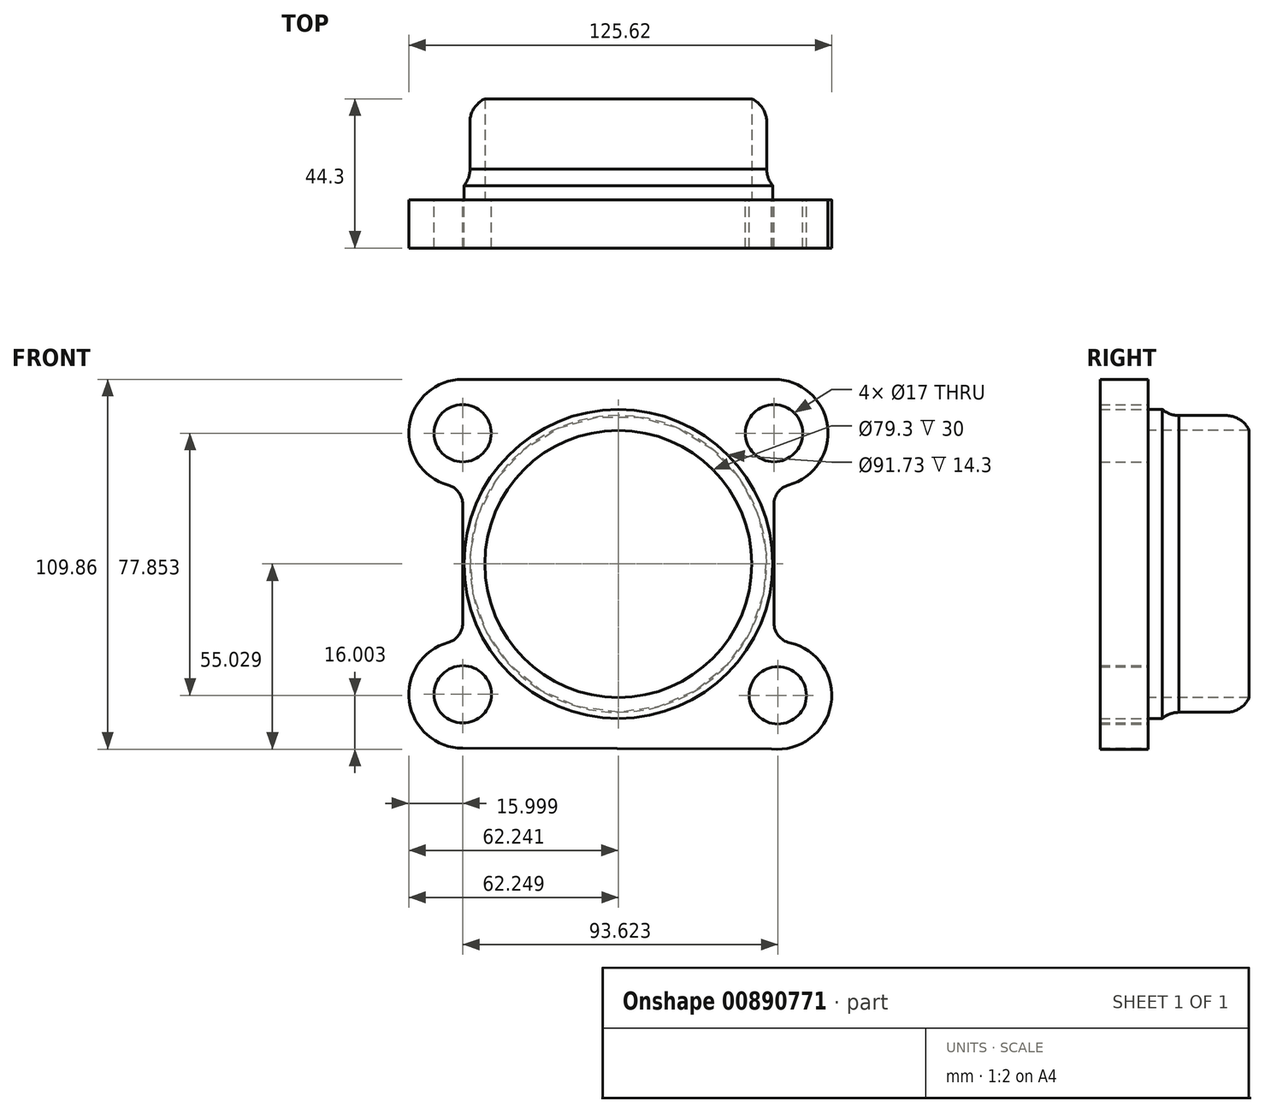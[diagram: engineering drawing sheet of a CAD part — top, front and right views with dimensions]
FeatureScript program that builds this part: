
annotation { "Feature Type Name" : "Feature", "Feature Type Description" : "" }
export const myFeature = defineFeature(function(context is Context, id is Id, definition is map)
    precondition{}
    {
        {
            var Q0;
            Q0=qCreatedBy(makeId("Front.planeOp"),FACE);
            var sketch = newSketch(context, id + "F0", { "sketchPlane" : qUnion([Q0])});
            skArc(sketch, "E0", {"start": v(-184.46, 80.5) * mm, "mid": v(-200.31, 66.69) * mm, "end": v(-188.8, 49.1) * mm});
            skArc(sketch, "E1", {"start": v(-188.8, 2.33) * mm, "mid": v(-200.28, -15.27) * mm, "end": v(-184.43, -29.06) * mm});
            skArc(sketch, "E2", {"start": v(-92.7, -29.25) * mm, "mid": v(-75.07, -16.05) * mm, "end": v(-87.31, 2.25) * mm});
            skArc(sketch, "E3", {"start": v(-87.62, 49.1) * mm, "mid": v(-76.11, 66.69) * mm, "end": v(-91.96, 80.5) * mm});
            skLineSegment(sketch, "E4", {"start": v(-184.43, 43.32) * mm, "end": v(-184.43, 8.1) * mm});
            skLineSegment(sketch, "E5", {"start": v(-92, 8.1) * mm, "end": v(-92, 43.32) * mm});
            skLineSegment(sketch, "E6", {"start": v(-184.46, 80.5) * mm, "end": v(-91.96, 80.5) * mm});
            skLineSegment(sketch, "E7", {"start": v(-184.43, -29.06) * mm, "end": v(-92.7, -29.25) * mm});
            skPoint(sketch, "E8.newPointA", {"position": v(-184.46, 48.5) * mm});
            skArc(sketch, "E8.filletArc", {"start": v(-184.43, 43.32) * mm, "mid": v(-185.65, 46.94) * mm, "end": v(-188.8, 49.1) * mm});
            skPoint(sketch, "E9.newPointA", {"position": v(-184.43, 2.94) * mm});
            skArc(sketch, "E9.filletArc", {"start": v(-188.8, 2.33) * mm, "mid": v(-185.64, 4.48) * mm, "end": v(-184.43, 8.1) * mm});
            skArc(sketch, "E10.filletArc", {"start": v(-92, 8.1) * mm, "mid": v(-90.68, 4.36) * mm, "end": v(-87.31, 2.25) * mm});
            skArc(sketch, "E11.filletArc", {"start": v(-87.62, 49.1) * mm, "mid": v(-90.77, 46.94) * mm, "end": v(-92, 43.32) * mm});
            skCircle(sketch, "E12", {"center": v(-138.21, 25.67) * mm, "radius": 44.08 * mm});
            skCircle(sketch, "E13", {"center": v(-138.21, 25.67) * mm, "radius": 45.87 * mm});
            skCircle(sketch, "E14", {"center": v(-184.46, 64.5) * mm, "radius": 8.5 * mm});
            skCircle(sketch, "E15", {"center": v(-91.96, 64.5) * mm, "radius": 8.5 * mm});
            skCircle(sketch, "E16", {"center": v(-90.84, -13.36) * mm, "radius": 8.5 * mm});
            skCircle(sketch, "E17", {"center": v(-184.43, -13.06) * mm, "radius": 8.5 * mm});
            skSolve(sketch);
        }
        {
            var Q0;
            Q0=makeQuery(id+"F0.imprint","IMPRINT",FACE,{"disambiguationData":[TD([[makeQuery(id+"F0.imprint","IMPRINT",EDGE,{"derivedFrom":sQuery(id+"F0.wireOp",EDGE,"E0")}),1.0]])]});
            var Q1;
            Q1=makeQuery(id+"F0.imprint","IMPRINT",FACE,{"disambiguationData":[TD([[makeQuery(id+"F0.imprint","IMPRINT",EDGE,{"derivedFrom":sQuery(id+"F0.wireOp",EDGE,"E1")}),1.0]])]});
            extrude(context, id + "F1", {"entities" : qUnion([Q0, Q1]), "depth" : 14.3 * mm, "offsetDistance" : 25.4 * mm});
        }
        {
            var Q0;
            Q0=makeQuery(id+"F0.imprint","IMPRINT",FACE,{"disambiguationData":[TD([[makeQuery(id+"F0.imprint","IMPRINT",EDGE,{"derivedFrom":sQuery(id+"F0.wireOp",EDGE,"E12")}),-1.0]])]});
            extrude(context, id + "F2", {"entities" : qUnion([Q0]), "oppositeDirection" : true, "depth" : 4.2 * mm, "offsetDistance" : 25.4 * mm});
        }
        {
            var Q0;
            Q0=makeQuery(id+"F0.imprint","IMPRINT",FACE,{"disambiguationData":[TD([[makeQuery(id+"F0.imprint","IMPRINT",EDGE,{"derivedFrom":sQuery(id+"F0.wireOp",EDGE,"E0")}),1.0]])]});
            var sketch = newSketch(context, id + "F3", { "sketchPlane" : qUnion([Q0])});
            skCircle(sketch, "E18", {"center": v(-138.22, 25.67) * mm, "radius": 44.08 * mm});
            skCircle(sketch, "E19", {"center": v(-138.22, 25.67) * mm, "radius": 39.65 * mm});
            skSolve(sketch);
        }
        {
            var Q0;
            Q0=makeQuery(id+"F3.imprint","IMPRINT",FACE,{"disambiguationData":[TD([[makeQuery(id+"F3.imprint","IMPRINT",EDGE,{"derivedFrom":sQuery(id+"F3.wireOp",EDGE,"E18")}),1.0]])]});
            extrude(context, id + "F4", {"entities" : qUnion([Q0]), "operationType" : NewBodyOperationType.ADD, "oppositeDirection" : true, "depth" : 30 * mm, "offsetDistance" : 25.4 * mm});
        }
        {
            var Q0;
            Q0=makeQuery(id+"F4.opExtrude","SWEPT_FACE",FACE,{"disambiguationData":[OSD([sQuery(id+"F3.wireOp",EDGE,"E18")])]});
            fillet(context, id + "F5", {"entities" : qUnion([Q0]), "radius" : 7.62 * mm, "tangentPropagation" : true, "allowEdgeOverflow" : false});
        }
    });
